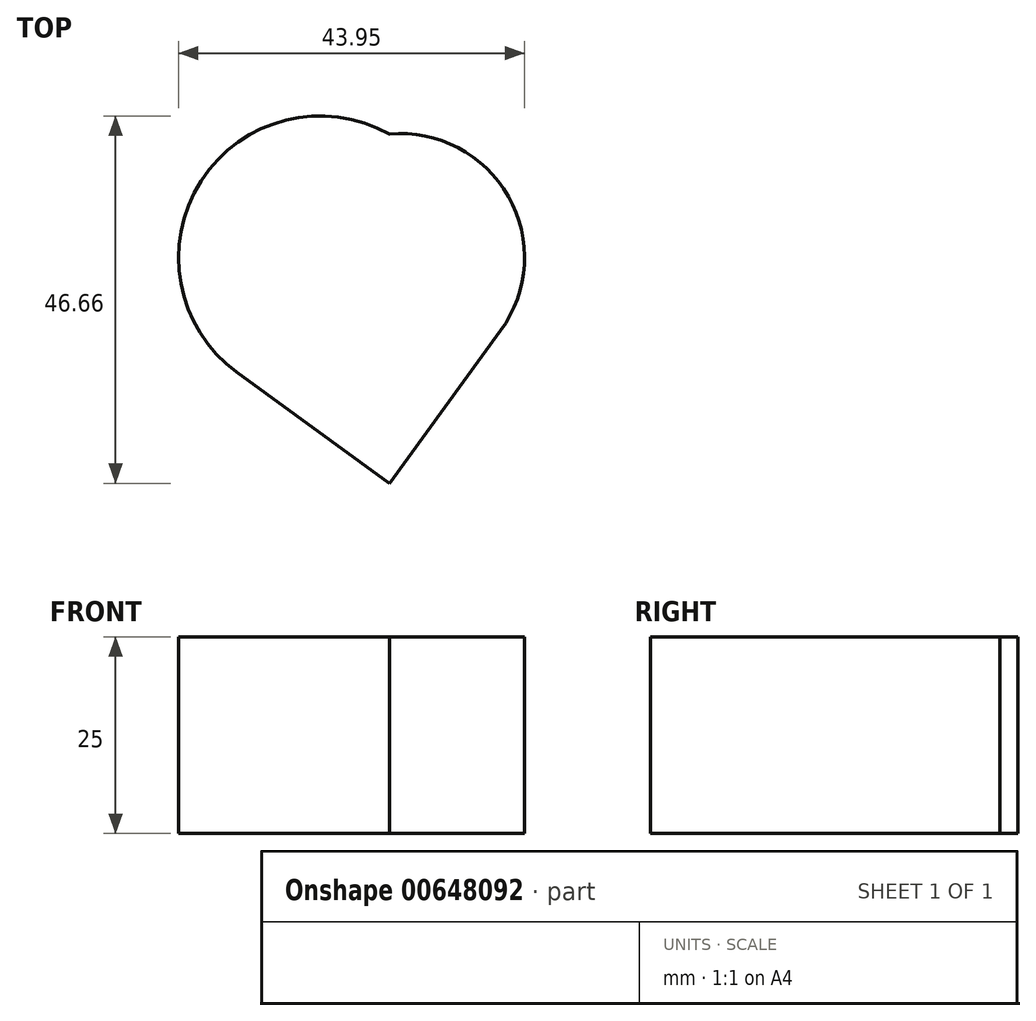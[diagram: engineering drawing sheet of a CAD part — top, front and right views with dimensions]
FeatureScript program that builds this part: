
annotation { "Feature Type Name" : "Feature", "Feature Type Description" : "" }
export const myFeature = defineFeature(function(context is Context, id is Id, definition is map)
    precondition{}
    {
        {
            var Q0;
            Q0=qCreatedBy(makeId("Top.planeOp"),FACE);
            var sketch = newSketch(context, id + "F0", { "sketchPlane" : qUnion([Q0])});
            skLineSegment(sketch, "E0", {"start": v(0, 0) * mm, "end": v(-19.4, 14.12) * mm});
            skLineSegment(sketch, "E1", {"start": v(0, 0) * mm, "end": v(14.12, 19.4) * mm});
            skArc(sketch, "E2", {"start": v(0, 44.36) * mm, "mid": v(-23.96, 38.39) * mm, "end": v(-19.4, 14.12) * mm});
            skArc(sketch, "E3", {"start": v(14.12, 19.4) * mm, "mid": v(15.1, 36.43) * mm, "end": v(0, 44.36) * mm});
            skSolve(sketch);
        }
        {
            var Q0;
            Q0=makeQuery(id+"F0.imprint","IMPRINT",FACE,{"disambiguationData":[TD([[makeQuery(id+"F0.imprint","IMPRINT",EDGE,{"derivedFrom":sQuery(id+"F0.wireOp",EDGE,"E0")}),-1.0]])]});
            extrude(context, id + "F1", {"entities" : qUnion([Q0]), "depth" : 25 * mm, "offsetDistance" : 25 * mm});
        }
    });
